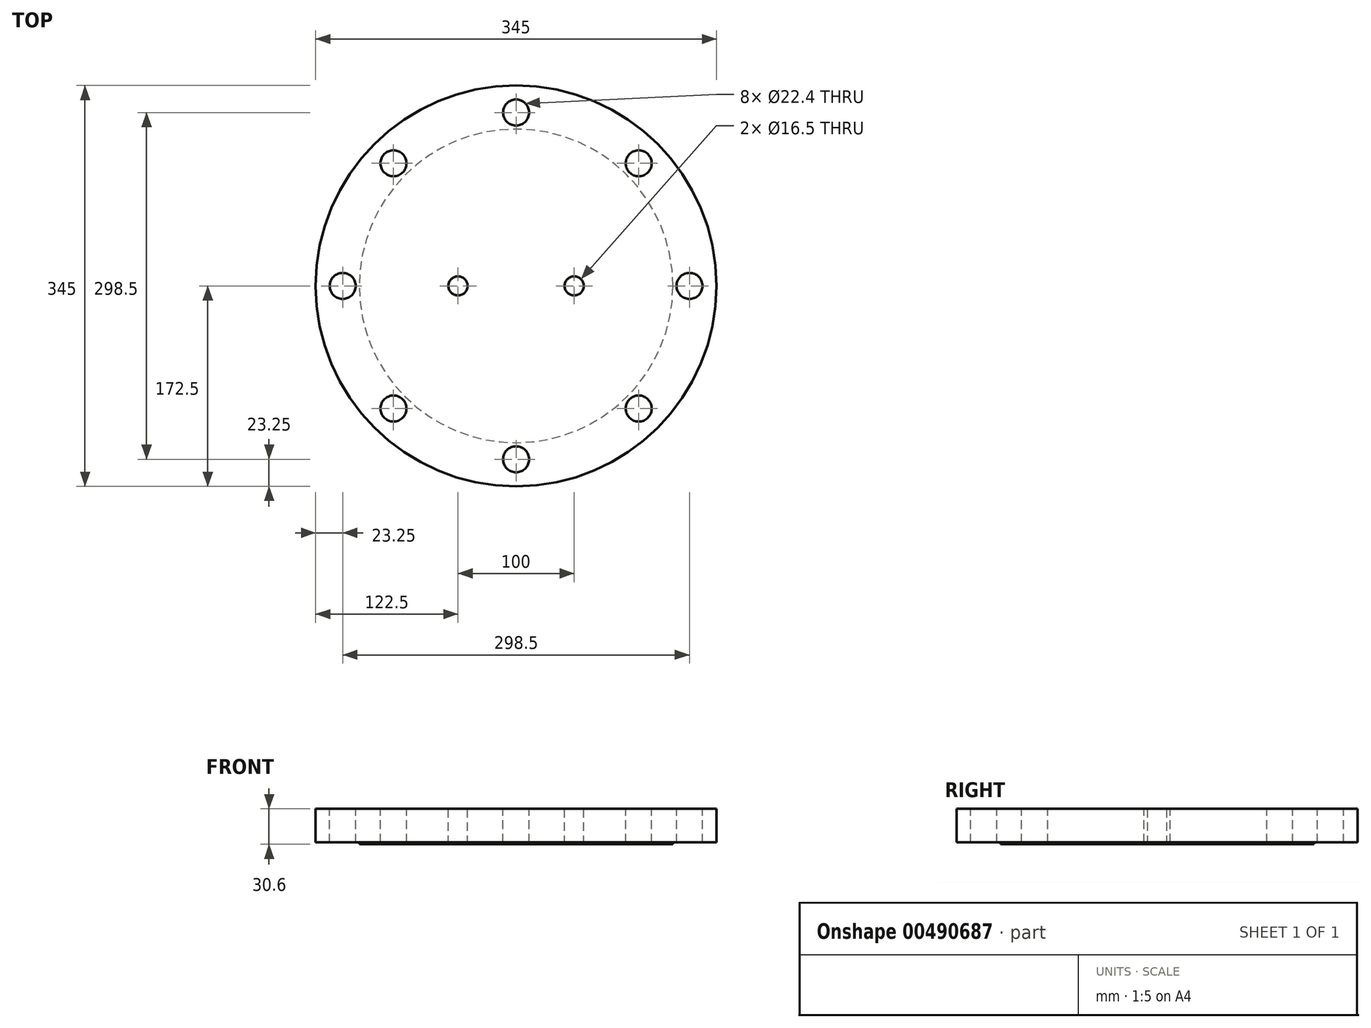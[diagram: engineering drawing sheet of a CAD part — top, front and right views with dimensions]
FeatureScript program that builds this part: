
annotation { "Feature Type Name" : "Feature", "Feature Type Description" : "" }
export const myFeature = defineFeature(function(context is Context, id is Id, definition is map)
    precondition{}
    {
        {
            var Q0;
            Q0=qCreatedBy(makeId("Top.planeOp"),FACE);
            var sketch = newSketch(context, id + "F0", { "sketchPlane" : qUnion([Q0])});
            skCircle(sketch, "E0", {"center": v(0, 0) * mm, "radius": 172.5 * mm});
            skSolve(sketch);
        }
        {
            var Q0;
            Q0 = qSketchRegion(id + "F0", true);
            extrude(context, id + "F1", {"entities" : qUnion([Q0]), "depth" : 29 * mm});
        }
        {
            var Q0;
            Q0=makeQuery(id+"F1.opExtrude","CAP_FACE",FACE,{"disambiguationData":[OSD([sQuery(id+"F0.wireOp",EDGE,"E0")])],"isStart":true});
            var sketch = newSketch(context, id + "F2", { "sketchPlane" : qUnion([Q0])});
            skCircle(sketch, "E1", {"center": v(0, 0) * mm, "radius": 134.95 * mm});
            skSolve(sketch);
        }
        {
            var Q0;
            Q0 = qSketchRegion(id + "F2", true);
            extrude(context, id + "F3", {"entities" : qUnion([Q0]), "operationType" : NewBodyOperationType.ADD, "depth" : 1.6 * mm});
        }
        {
            var Q0;
            Q0=makeQuery(id+"F1.opExtrude","CAP_FACE",FACE,{"disambiguationData":[OSD([sQuery(id+"F0.wireOp",EDGE,"E0")])],"isStart":false});
            var sketch = newSketch(context, id + "F4", { "sketchPlane" : qUnion([Q0])});
            skCircle(sketch, "E2", {"center": v(0, 0) * mm, "radius": 149.25 * mm, "construction": true});
            skCircle(sketch, "E3", {"center": v(0, 149.25) * mm, "radius": 11.2 * mm});
            skCircle(sketch, "E4.1.0", {"center": v(-105.54, 105.54) * mm, "radius": 11.2 * mm});
            skCircle(sketch, "E4.2.0", {"center": v(-149.25, 0) * mm, "radius": 11.2 * mm});
            skCircle(sketch, "E5.1.3.0", {"center": v(-105.54, -105.54) * mm, "radius": 11.2 * mm});
            skCircle(sketch, "E5.1.4.0", {"center": v(0, -149.25) * mm, "radius": 11.2 * mm});
            skCircle(sketch, "E5.1.5.0", {"center": v(105.54, -105.54) * mm, "radius": 11.2 * mm});
            skCircle(sketch, "E5.1.6.0", {"center": v(149.25, 0) * mm, "radius": 11.2 * mm});
            skCircle(sketch, "E5.1.7.0", {"center": v(105.54, 105.54) * mm, "radius": 11.2 * mm});
            skSolve(sketch);
        }
        {
            var Q0;
            Q0 = qSketchRegion(id + "F4", true);
            extrude(context, id + "F5", {"entities" : qUnion([Q0]), "operationType" : NewBodyOperationType.REMOVE, "endBound" : BoundingType.THROUGH_ALL, "oppositeDirection" : true, "depth" : 25 * mm});
        }
        {
            var Q0;
            Q0=makeQuery(id+"F1.opExtrude","CAP_FACE",FACE,{"disambiguationData":[OSD([sQuery(id+"F0.wireOp",EDGE,"E0")])],"isStart":false});
            var sketch = newSketch(context, id + "F6", { "sketchPlane" : qUnion([Q0])});
            skCircle(sketch, "E6", {"center": v(-50, 0) * mm, "radius": 8.25 * mm});
            skCircle(sketch, "E7", {"center": v(50, 0) * mm, "radius": 8.25 * mm});
            skSolve(sketch);
        }
        {
            var Q0;
            Q0 = qSketchRegion(id + "F6", true);
            extrude(context, id + "F7", {"entities" : qUnion([Q0]), "operationType" : NewBodyOperationType.REMOVE, "endBound" : BoundingType.THROUGH_ALL, "oppositeDirection" : true, "depth" : 25 * mm});
        }
    });
